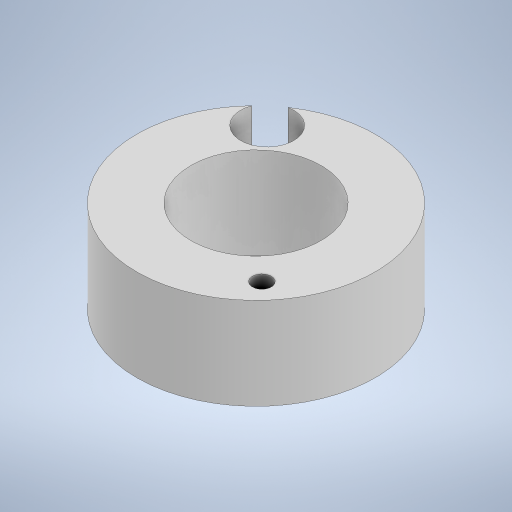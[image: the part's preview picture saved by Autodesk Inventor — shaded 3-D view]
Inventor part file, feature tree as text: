
AUTODESK INVENTOR PART (.ipt)
format: ipt  version: 2024.2 (Build 282272000, 272)  size: 241,152 bytes
history: native  units: mm
features: other x1, extrude x1, sketch x1
ambient origin geometry x8: Origin, YZ Plane, XZ Plane, XY Plane, X Axis, Y Axis, Z Axis, Center Point
bodies: Body1 (feature_tree)
feature tree (3):
  other  "Твердое тело1"
  extrude  "Выдавливание1"  Depth=26.0mm
  sketch  "Эскиз1"
